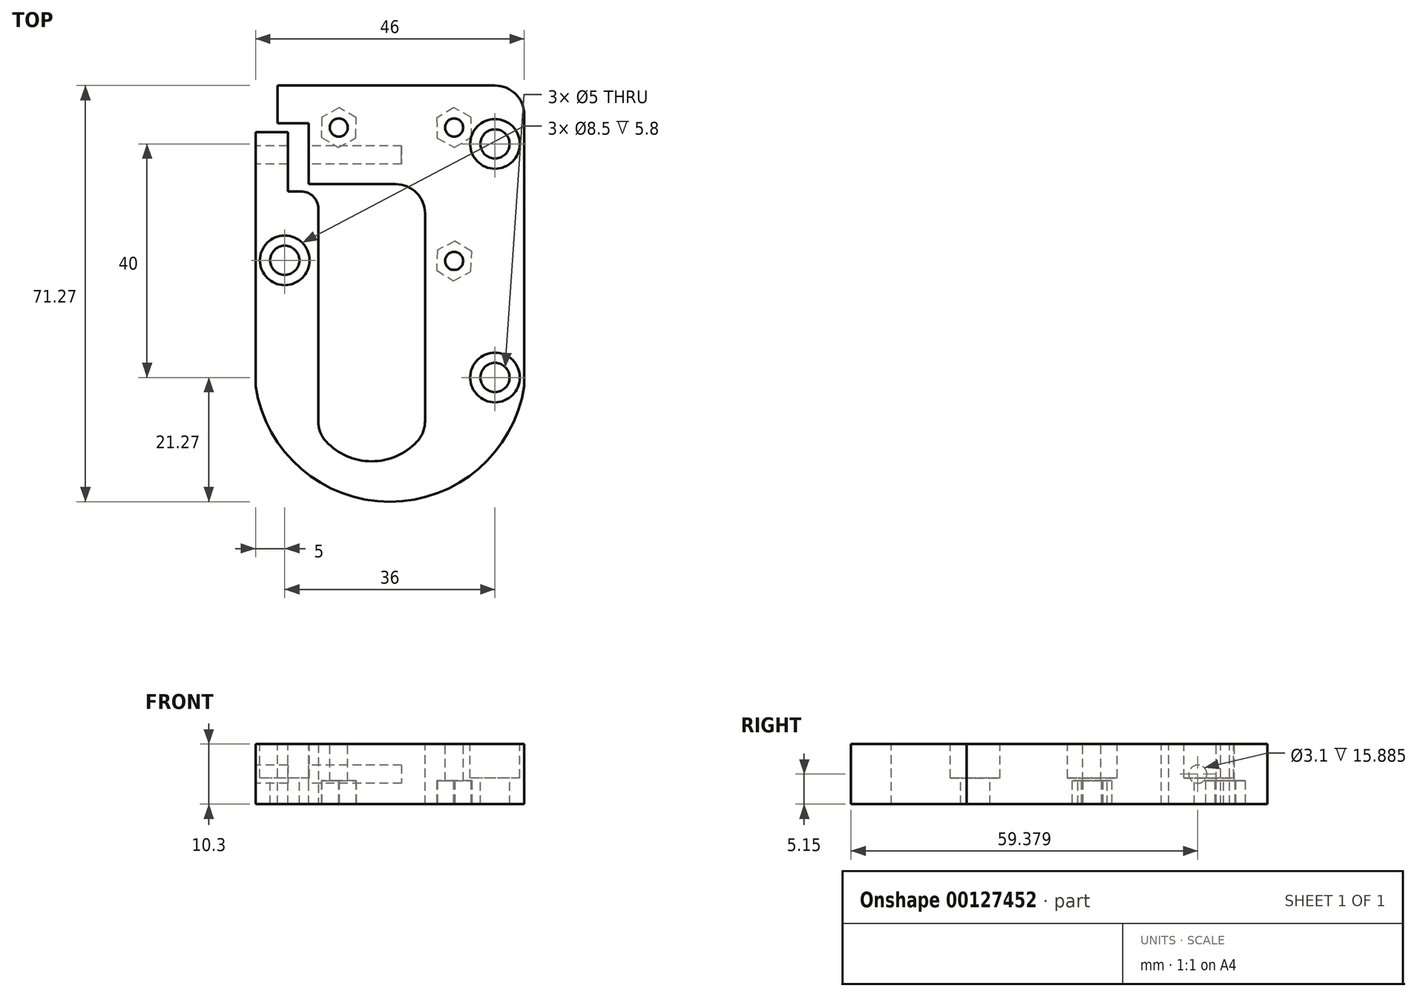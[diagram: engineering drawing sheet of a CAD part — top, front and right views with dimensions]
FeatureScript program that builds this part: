
annotation { "Feature Type Name" : "Feature", "Feature Type Description" : "" }
export const myFeature = defineFeature(function(context is Context, id is Id, definition is map)
    precondition{}
    {
        {
            var Q0;
            Q0=qCreatedBy(makeId("Top.planeOp"),FACE);
            var sketch = newSketch(context, id + "F0", { "sketchPlane" : qUnion([Q0])});
            skLineSegment(sketch, "E0.top", {"start": v(23, 35.75) * mm, "end": v(-23, 35.75) * mm});
            skPoint(sketch, "E0.middle", {"position": v(0, 0) * mm});
            skArc(sketch, "E1", {"start": v(-23, -15.75) * mm, "mid": v(0, -35.52) * mm, "end": v(23, -15.75) * mm});
            skLineSegment(sketch, "E2", {"start": v(-23, -15.75) * mm, "end": v(-23, 35.75) * mm});
            skLineSegment(sketch, "E3", {"start": v(23, -15.75) * mm, "end": v(23, 35.75) * mm});
            skSolve(sketch);
        }
        {
            var Q0;
            Q0 = qSketchRegion(id + "F0", true);
            extrude(context, id + "F1", {"entities" : qUnion([Q0]), "depth" : 10.3 * mm});
        }
        {
            var Q0;
            Q0=makeQuery(id+"F1.opExtrude","CAP_FACE",FACE,{"disambiguationData":[OSD([sQuery(id+"F0.wireOp",EDGE,"E0.top"),sQuery(id+"F0.wireOp",EDGE,"E1"),sQuery(id+"F0.wireOp",EDGE,"E2"),sQuery(id+"F0.wireOp",EDGE,"E3")])],"isStart":false});
            var sketch = newSketch(context, id + "F2", { "sketchPlane" : qUnion([Q0])});
            skCircle(sketch, "E4", {"center": v(11, 28.55) * mm, "radius": 1.55 * mm});
            skCircle(sketch, "E5", {"center": v(-8.75, 28.55) * mm, "radius": 1.55 * mm});
            skCircle(sketch, "E6", {"center": v(11, 5.72) * mm, "radius": 1.55 * mm});
            skCircle(sketch, "E7", {"center": v(18, 25.75) * mm, "radius": 2.5 * mm});
            skCircle(sketch, "E8", {"center": v(18, -14.25) * mm, "radius": 2.5 * mm});
            skCircle(sketch, "E9", {"center": v(-18, 5.82) * mm, "radius": 2.5 * mm});
            skLineSegment(sketch, "E10.bottom", {"start": v(6.01, 17.63) * mm, "end": v(-12.26, 17.63) * mm});
            skLineSegment(sketch, "E10.top", {"start": v(6.01, -23.43) * mm, "end": v(-12.26, -23.43) * mm});
            skLineSegment(sketch, "E10.left", {"start": v(6.01, 17.63) * mm, "end": v(6.01, -23.43) * mm});
            skLineSegment(sketch, "E10.right", {"start": v(-12.26, 17.63) * mm, "end": v(-12.26, -23.43) * mm});
            skArc(sketch, "E11", {"start": v(-12.26, -23.43) * mm, "mid": v(-3.12, -28.6) * mm, "end": v(6.01, -23.43) * mm});
            skLineSegment(sketch, "E12", {"start": v(-12.26, 17.63) * mm, "end": v(-15.59, 17.63) * mm});
            skLineSegment(sketch, "E13", {"start": v(-12.26, 18.86) * mm, "end": v(6.01, 18.86) * mm});
            skLineSegment(sketch, "E14", {"start": v(6.01, 18.86) * mm, "end": v(6.01, 17.63) * mm});
            skLineSegment(sketch, "E15.bottom", {"start": v(-15.59, 29.31) * mm, "end": v(-23, 29.31) * mm});
            skLineSegment(sketch, "E15.right", {"start": v(-23, 29.31) * mm, "end": v(-23, 27.75) * mm});
            skLineSegment(sketch, "E16.bottom", {"start": v(-23, 29.31) * mm, "end": v(-19.25, 29.31) * mm});
            skLineSegment(sketch, "E16.top", {"start": v(-23, 35.75) * mm, "end": v(-19.25, 35.75) * mm});
            skLineSegment(sketch, "E16.left", {"start": v(-23, 29.31) * mm, "end": v(-23, 35.75) * mm});
            skLineSegment(sketch, "E16.right", {"start": v(-19.25, 29.31) * mm, "end": v(-19.25, 35.75) * mm});
            skLineSegment(sketch, "E17", {"start": v(-17.48, 27.75) * mm, "end": v(-17.48, 17.63) * mm});
            skLineSegment(sketch, "E18", {"start": v(-17.48, 17.63) * mm, "end": v(-15.59, 17.63) * mm});
            skLineSegment(sketch, "E19", {"start": v(-12.26, 18.86) * mm, "end": v(-13.89, 18.86) * mm});
            skLineSegment(sketch, "E20", {"start": v(-13.89, 18.86) * mm, "end": v(-13.89, 29.31) * mm});
            skLineSegment(sketch, "E21", {"start": v(-15.59, 29.31) * mm, "end": v(-13.89, 29.31) * mm});
            skLineSegment(sketch, "E22", {"start": v(-17.48, 27.75) * mm, "end": v(-23, 27.75) * mm});
            skSolve(sketch);
        }
        {
            var Q0;
            Q0 = qSketchRegion(id + "F2", true);
            extrude(context, id + "F3", {"entities" : qUnion([Q0]), "operationType" : NewBodyOperationType.REMOVE, "endBound" : BoundingType.UP_TO_NEXT, "oppositeDirection" : true, "depth" : 25 * mm});
        }
        {
            var Q0;
            Q0=makeQuery(id+"F3.boolean.opBoolean","COPY",EDGE,{"derivedFrom":makeQuery(id+"F3.opExtrude","SWEPT_EDGE",EDGE,{"disambiguationData":[OSD([sQuery(id+"F2.wireOp",EDGE,"E10.bottom"),sQuery(id+"F2.wireOp",EDGE,"E10.right"),sQuery(id+"F2.wireOp",EDGE,"E12")])]})});
            fillet(context, id + "F4", {"entities" : qUnion([Q0]), "radius" : 3 * mm, "tangentPropagation" : true, "allowEdgeOverflow" : false});
        }
        {
            var Q0;
            Q0=makeQuery(id+"F3.boolean.opBoolean","COPY",EDGE,{"derivedFrom":makeQuery(id+"F3.opExtrude","SWEPT_EDGE",EDGE,{"disambiguationData":[OSD([sQuery(id+"F0.wireOp",EDGE,"E0.top"),sQuery(id+"F2.wireOp",EDGE,"E16.top"),sQuery(id+"F2.wireOp",EDGE,"E16.right")])]})});
            var Q1;
            Q1=makeQuery(id+"F1.opExtrude","SWEPT_EDGE",EDGE,{"disambiguationData":[OSD([sQuery(id+"F0.wireOp",EDGE,"E0.top"),sQuery(id+"F0.wireOp",EDGE,"E3")])]});
            var Q2;
            Q2=makeQuery(id+"F3.boolean.opBoolean","COPY",EDGE,{"derivedFrom":makeQuery(id+"F3.opExtrude","SWEPT_EDGE",EDGE,{"disambiguationData":[OSD([sQuery(id+"F2.wireOp",EDGE,"E10.top"),sQuery(id+"F2.wireOp",EDGE,"E10.right"),sQuery(id+"F2.wireOp",EDGE,"E11")])]})});
            var Q3;
            Q3=makeQuery(id+"F3.boolean.opBoolean","COPY",EDGE,{"derivedFrom":makeQuery(id+"F3.opExtrude","SWEPT_EDGE",EDGE,{"disambiguationData":[OSD([sQuery(id+"F2.wireOp",EDGE,"E10.top"),sQuery(id+"F2.wireOp",EDGE,"E10.left"),sQuery(id+"F2.wireOp",EDGE,"E11")])]})});
            var Q4;
            Q4=makeQuery(id+"F3.boolean.opBoolean","COPY",EDGE,{"derivedFrom":makeQuery(id+"F3.opExtrude","SWEPT_EDGE",EDGE,{"disambiguationData":[OSD([sQuery(id+"F2.wireOp",EDGE,"E13"),sQuery(id+"F2.wireOp",EDGE,"E14")])]})});
            fillet(context, id + "F5", {"entities" : qUnion([Q0, Q1, Q2, Q3, Q4]), "radius" : 5 * mm, "tangentPropagation" : true, "allowEdgeOverflow" : false});
        }
        {
            var Q0;
            Q0=makeQuery(id+"F1.opExtrude","CAP_FACE",FACE,{"disambiguationData":[OSD([sQuery(id+"F0.wireOp",EDGE,"E0.top"),sQuery(id+"F0.wireOp",EDGE,"E1"),sQuery(id+"F0.wireOp",EDGE,"E2"),sQuery(id+"F0.wireOp",EDGE,"E3")])],"isStart":false});
            var sketch = newSketch(context, id + "F6", { "sketchPlane" : qUnion([Q0])});
            skCircle(sketch, "E23", {"center": v(18, 25.75) * mm, "radius": 4.25 * mm});
            skCircle(sketch, "E24", {"center": v(-18, 5.82) * mm, "radius": 4.25 * mm});
            skCircle(sketch, "E25", {"center": v(18, -14.25) * mm, "radius": 4.25 * mm});
            skSolve(sketch);
        }
        {
            var Q0;
            Q0 = qSketchRegion(id + "F6", true);
            extrude(context, id + "F7", {"entities" : qUnion([Q0]), "operationType" : NewBodyOperationType.REMOVE, "oppositeDirection" : true, "depth" : 5.8 * mm});
        }
        {
            var Q0;
            Q0=makeQuery(id+"F1.opExtrude","SWEPT_FACE",FACE,{"disambiguationData":[OSD([sQuery(id+"F0.wireOp",EDGE,"E2")])]});
            var sketch = newSketch(context, id + "F8", { "sketchPlane" : qUnion([Q0])});
            skCircle(sketch, "E26", {"center": v(-23.86, 5.15) * mm, "radius": 1.55 * mm});
            skPoint(sketch, "E26.centerSnap0", {"position": v(-27.75, 5.15) * mm});
            skSolve(sketch);
        }
        {
            var Q0;
            Q0 = qSketchRegion(id + "F8", true);
            extrude(context, id + "F9", {"entities" : qUnion([Q0]), "operationType" : NewBodyOperationType.REMOVE, "oppositeDirection" : true, "depth" : 25 * mm});
        }
        {
            var Q0;
            Q0=makeQuery(id+"F1.opExtrude","CAP_FACE",FACE,{"disambiguationData":[OSD([sQuery(id+"F0.wireOp",EDGE,"E0.top"),sQuery(id+"F0.wireOp",EDGE,"E1"),sQuery(id+"F0.wireOp",EDGE,"E2"),sQuery(id+"F0.wireOp",EDGE,"E3")])],"isStart":true});
            var sketch = newSketch(context, id + "F10", { "sketchPlane" : qUnion([Q0])});
            skCircle(sketch, "E27.cCircle", {"center": v(11, -28.55) * mm, "radius": 2.95 * mm, "construction": true});
            skLineSegment(sketch, "E27.0", {"start": v(8.1, -26.77) * mm, "end": v(11.09, -25.14) * mm});
            skLineSegment(sketch, "E27.1", {"start": v(11.09, -25.14) * mm, "end": v(14, -26.92) * mm});
            skLineSegment(sketch, "E27.2", {"start": v(14, -26.92) * mm, "end": v(13.9, -30.33) * mm});
            skLineSegment(sketch, "E27.3", {"start": v(13.9, -30.33) * mm, "end": v(10.91, -31.96) * mm});
            skLineSegment(sketch, "E27.4", {"start": v(10.91, -31.96) * mm, "end": v(8, -30.18) * mm});
            skLineSegment(sketch, "E27.5", {"start": v(8, -30.18) * mm, "end": v(8.1, -26.77) * mm});
            skPoint(sketch, "E27.0.midPoint", {"position": v(9.59, -25.96) * mm});
            skCircle(sketch, "E28.cCircle", {"center": v(-8.75, -28.55) * mm, "radius": 2.95 * mm, "construction": true});
            skLineSegment(sketch, "E28.0", {"start": v(-11.72, -26.88) * mm, "end": v(-8.8, -25.14) * mm});
            skLineSegment(sketch, "E28.1", {"start": v(-8.8, -25.14) * mm, "end": v(-5.82, -26.81) * mm});
            skLineSegment(sketch, "E28.2", {"start": v(-5.82, -26.81) * mm, "end": v(-5.78, -30.22) * mm});
            skLineSegment(sketch, "E28.3", {"start": v(-5.78, -30.22) * mm, "end": v(-8.7, -31.96) * mm});
            skLineSegment(sketch, "E28.4", {"start": v(-8.7, -31.96) * mm, "end": v(-11.68, -30.29) * mm});
            skLineSegment(sketch, "E28.5", {"start": v(-11.68, -30.29) * mm, "end": v(-11.72, -26.88) * mm});
            skPoint(sketch, "E28.0.midPoint", {"position": v(-10.26, -26.01) * mm});
            skCircle(sketch, "E29.cCircle", {"center": v(11, -5.72) * mm, "radius": 2.95 * mm, "construction": true});
            skLineSegment(sketch, "E29.0", {"start": v(7.98, -4.14) * mm, "end": v(10.85, -2.31) * mm});
            skLineSegment(sketch, "E29.1", {"start": v(10.85, -2.31) * mm, "end": v(13.87, -3.89) * mm});
            skLineSegment(sketch, "E29.2", {"start": v(13.87, -3.89) * mm, "end": v(14.02, -7.3) * mm});
            skLineSegment(sketch, "E29.3", {"start": v(14.02, -7.3) * mm, "end": v(11.15, -9.12) * mm});
            skLineSegment(sketch, "E29.4", {"start": v(11.15, -9.12) * mm, "end": v(8.13, -7.55) * mm});
            skLineSegment(sketch, "E29.5", {"start": v(8.13, -7.55) * mm, "end": v(7.98, -4.14) * mm});
            skPoint(sketch, "E29.0.midPoint", {"position": v(9.42, -3.23) * mm});
            skSolve(sketch);
        }
        {
            var Q0;
            Q0 = qSketchRegion(id + "F10", true);
            extrude(context, id + "F11", {"entities" : qUnion([Q0]), "operationType" : NewBodyOperationType.REMOVE, "oppositeDirection" : true, "depth" : 4 * mm});
        }
    });
